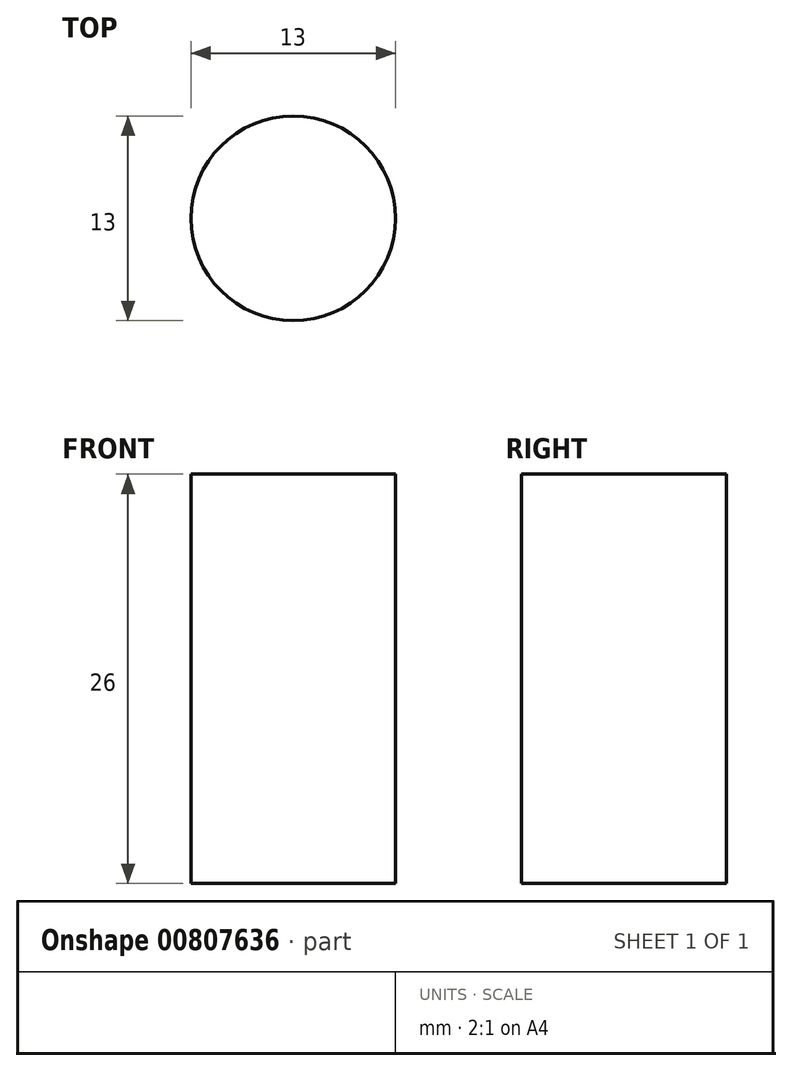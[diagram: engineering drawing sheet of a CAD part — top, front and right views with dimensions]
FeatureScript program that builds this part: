
annotation { "Feature Type Name" : "Feature", "Feature Type Description" : "" }
export const myFeature = defineFeature(function(context is Context, id is Id, definition is map)
    precondition{}
    {
        {
            var Q0;
            Q0=qCreatedBy(makeId("Top.planeOp"),FACE);
            var sketch = newSketch(context, id + "F0", { "sketchPlane" : qUnion([Q0])});
            skCircle(sketch, "E0", {"center": v(0, 0) * mm, "radius": 6.5 * mm});
            skSolve(sketch);
        }
        {
            var Q0;
            Q0 = qSketchRegion(id + "F0", true);
            extrude(context, id + "F1", {"entities" : qUnion([Q0]), "depth" : 26 * mm, "offsetDistance" : 25 * mm});
        }
    });
